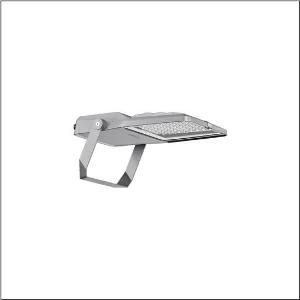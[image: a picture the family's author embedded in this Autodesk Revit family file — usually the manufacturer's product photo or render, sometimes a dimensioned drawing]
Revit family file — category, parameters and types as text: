
# Revit family: floodlight_fl_21_iq_mini___pl64_5xa7772c1e1a_659a
name_source: partatom
category: Lighting Fixtures
units: mm (PartAtom-declared; Revit-internal decimal feet)

## family parameters
Cut with Voids When Loaded = No
Host = Face
Light Source = No
Part Type = Normal
Room Calculation Point = No
Round Connector Dimension = Use Diameter
Shared = No

## types (1)
- --- (1 x LED, 9770 lm, 87.2 W, 2200K)
    Apparent Load = 87 VA
    CIE Flux Codes = 28 80 98 100 100
    Color Rendering = 70
    Color Temperature = 2200K
    Default Elevation = 1800 mm
    Description = Floodlight FL 21 iQ mini, floodlight, primary light control with lens, of PMMA, primary optical cover: protective disc, of toughened safety glass, transparent, light distribution: PL64, light emission: direct distribution, installation type: surface-mounted, LED, High Power LED, rated luminous flux: 9.770lm, luminous efficacy: 112lm/W, light colour: 722, colour temperature: 2200K, control: Street-Remote, Auto-Match, Temp-Guard, Night-Set, Smart-Wire, Desk-Remote (wireless, voltage-free reading and setting of iQ features in the workshop via application-optimized NFC function/RFID function), optimised constant luminous flux control (CLO 2.0), with terminal, 6-pole, mains connection: 220..240V, AC, 50/60Hz, start of lifetime: 87W, end of service life: 92W, reduction: 40W, luminaire housing, of diecast aluminium, powder-coated, Siteco® metallic grey (DB 702S), corrosivity category C5 mid according to DIN EN ISO 12944, sealing non-destructively replaceable, mounting bracket, of steel, galvanised, powder-coated, Siteco® metallic grey (DB 702S), protection rating (complete): IP66, insulation class (complete): insulation class II (safety insulation), certification: CE, ENEC, VDE, protection symbol: D, impact resistance: IK08, permissible operating ambient temperature: -40..+40°C, permissible operating ambient temperature for outdoor applications: -40..+50°C, standard: DIN EN 12944, LABS conformity tested according to VDMA 24364:2018-05, packaging unit: 1 piece

Light Distribution: PL64
    Height = 70 mm
    Lamp = 1 x LED
    Lamp Light Flux = 9770 lm
    Lamp Power = 87.2 W
    Lamp count = 1
    Length = 485 mm
    Luminous efficacy = 112 lm/W
    Manufacturer = Siteco
    ModVariant = No
    Model = 5XA7772C1E1A
    Number of Poles = 1
    OnlyDefault = Yes
    Power Factor = 1
    Product Name = Floodlight FL 21 iQ mini | PL64
    Product group = floodlight | pylon annexe
    ProductGroupID = 6200
    Protection Class = Protection class II
    Protection Degree = IP 66
    RLX_Detail_Level = 1
    RLX_Emergency_Light_Flux = 0 lm
    RLX_Emergency_Type = 0
    RLX_Emergency_Type_DB = No
    RlxData = <blob elided: 96233 chars, md5=c272b5a2>
    Socket = socket
    Standby Power = 0 W
    System Light Flux = 9770 lm
    System Power = 87 W
    Type Comments = factory setting: luminous flux: 100 % | dim-lin: 254 | 456 mA
    Type Image = l_1006845.jpg
    URL = http://relux.com
    VarID = @adj_098769
    Voltage = 0 V
    Weight = 0.00 kg
    Width = 337 mm

## geometry (parser evidence)
native form markers: Blend x4, Sweep x10
no freeform markers — native parametric forms only
